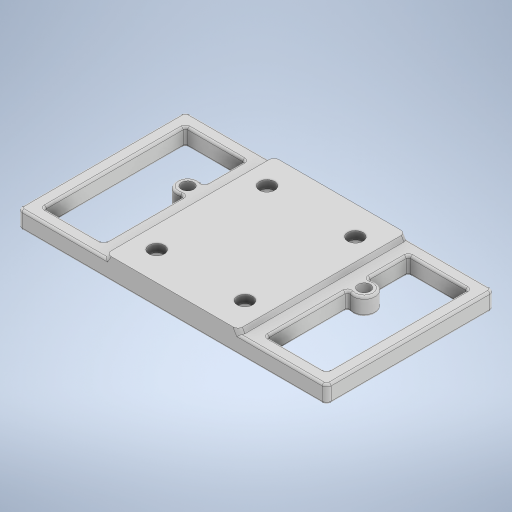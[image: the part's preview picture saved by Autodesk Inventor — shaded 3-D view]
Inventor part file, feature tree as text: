
AUTODESK INVENTOR PART (.ipt)
format: ipt  version: 2024.2 (Build 282272000, 272)  size: 457,216 bytes
history: native  units: mm
features: sketch x7, extrude x5, fillet x3, chamfer x2, hole x2
ambient origin geometry x8: Origin, YZ Plane, XZ Plane, XY Plane, X Axis, Y Axis, Z Axis, Center Point
bodies: Solid1 (feature_tree)
feature tree (19):
  extrude  "Extrusion1"  Depth=38.0mm
  extrude  "Extrusion2"  Depth=2.0mm
  chamfer  "Chamfer2"  Distance=1.0mm
  chamfer  "Chamfer3"  Distance=1.0mm Angle=30.0deg
  fillet  "Fillet1"  Radius=1.0mm
  hole  "Hole1"  [1 undecoded]
  extrude  "Extrusion4"  Depth=25.0mm
  hole  "Hole2"  [1 undecoded]
  extrude  "Extrusion5"  Depth=0.2mm
  fillet  "Fillet5"  Radius=2.8mm
  fillet  "Fillet3"  Radius=55.0mm
  extrude  "Extrusion6"  Depth=0.2mm
  sketch  "Sketch1"  dims[d0=70.0mm d1=38.0mm]
  sketch  "Sketch2"  dims[d2=4.0mm d3=0.0mm d4=31.0mm d5=1.0mm d6=0.0mm d10=1.0mm d11=2.0mm d12=30.0deg]
  sketch  "Sketch4"  dims[d13=1.0mm d14=2.0mm d15=30.0deg d16=1.0mm]
  sketch  "Sketch5"  dims[d27=0.5mm d29=3.5mm]
  sketch  "Sketch6"  dims[d30=20.0mm d31=25.0mm]
  sketch  "Sketch9"  dims[d32=45.0mm d33=31.5mm]
  sketch  "Sketch10"  dims[d34=3.5mm d35=6.0mm d36=5.25mm d37=3.0mm d38=90.0deg d39=8.0mm d40=20.594885mm d41=40.0mm d42=2.8mm d43=55.0mm d44=24.0mm d48=4.5mm d49=4.5mm d50=10.0mm d51=0.0mm d52=40.0mm d53=2.8mm d55=55.0mm d56=23.5mm d57=2.8mm d58=6.0mm d59=5.25mm d60=3.0mm d61=90.0deg d62=8.0mm d63=20.594885mm d64=3.0mm d65=3.0mm d66=3.0mm d67=3.0mm d68=3.0mm d69=3.0mm d70=5.0mm d71=0.0mm d72=0.0mm d73=0.5mm d74=0.2mm d75=0.0mm d28=0.0mm]
note: 2 required parameter values undecoded (feature->parameter linkage not recoverable at this tier; creation-order binding heuristic only, values carry confidence <= 0.55)
